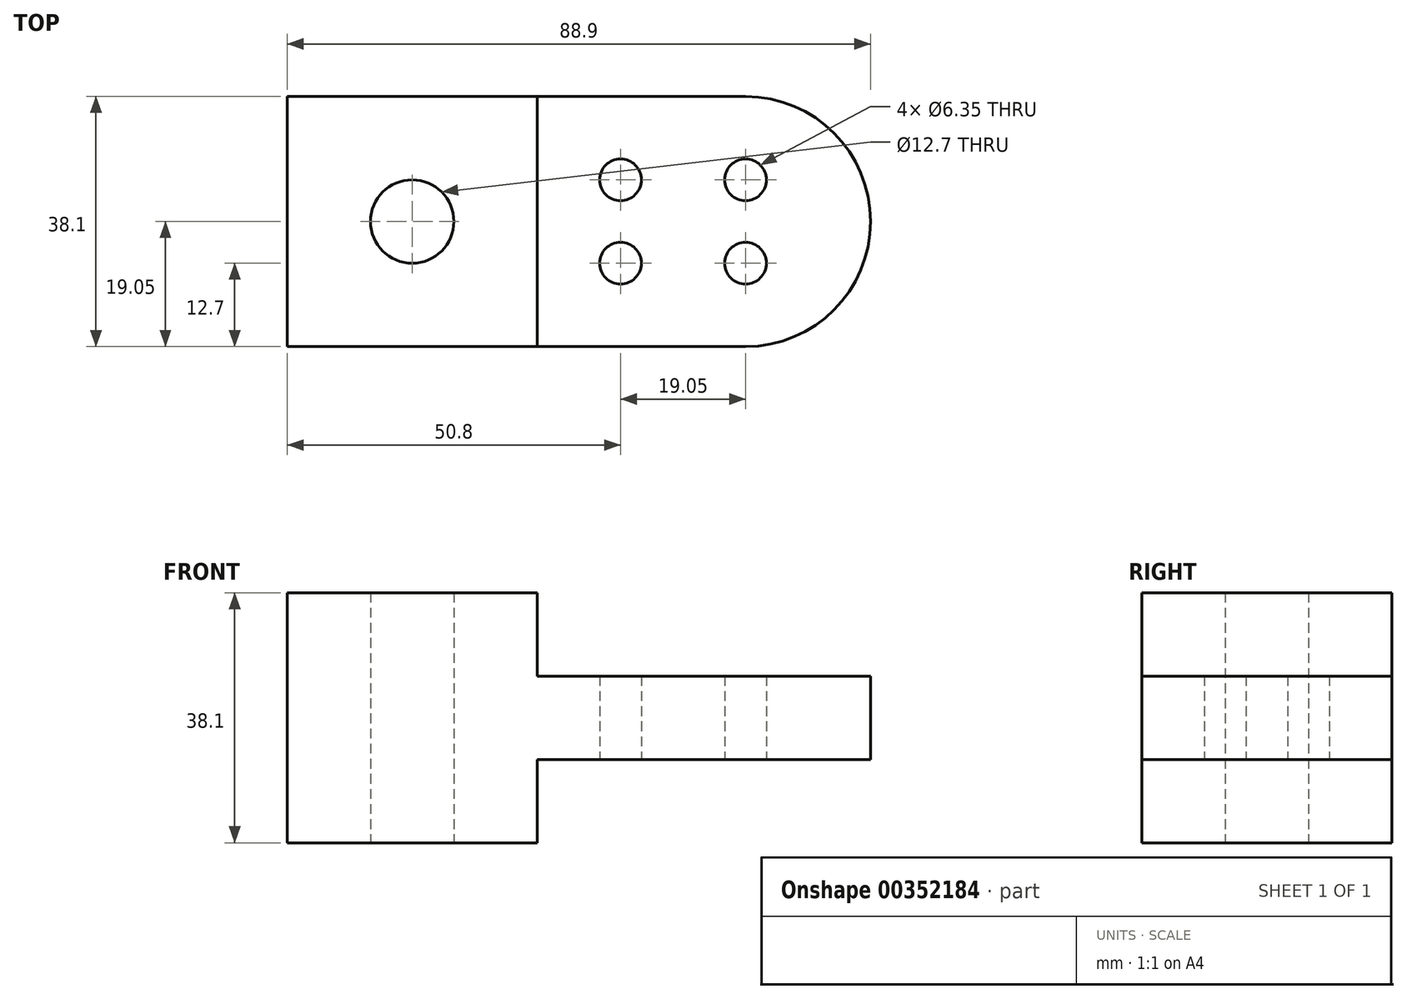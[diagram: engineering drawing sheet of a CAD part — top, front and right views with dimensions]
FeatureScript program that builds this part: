
annotation { "Feature Type Name" : "Feature", "Feature Type Description" : "" }
export const myFeature = defineFeature(function(context is Context, id is Id, definition is map)
    precondition{}
    {
        {
            var Q0;
            Q0=qCreatedBy(makeId("Top.planeOp"),FACE);
            var sketch = newSketch(context, id + "F0", { "sketchPlane" : qUnion([Q0])});
            skLineSegment(sketch, "E0.bottom", {"start": v(-38.1, 19.05) * mm, "end": v(0, 19.05) * mm});
            skLineSegment(sketch, "E0.top", {"start": v(-38.1, -19.05) * mm, "end": v(0, -19.05) * mm});
            skLineSegment(sketch, "E0.left", {"start": v(-38.1, 19.05) * mm, "end": v(-38.1, -19.05) * mm});
            skLineSegment(sketch, "E0.right", {"start": v(0, 19.05) * mm, "end": v(0, -19.05) * mm});
            skLineSegment(sketch, "E1", {"start": v(0, 19.05) * mm, "end": v(31.75, 19.05) * mm});
            skLineSegment(sketch, "E2", {"start": v(0, -19.05) * mm, "end": v(31.75, -19.05) * mm});
            skArc(sketch, "E3", {"start": v(31.75, 19.05) * mm, "mid": v(50.8, 0) * mm, "end": v(31.75, -19.05) * mm});
            skCircle(sketch, "E4", {"center": v(-19.05, 0) * mm, "radius": 6.35 * mm});
            skCircle(sketch, "E5", {"center": v(12.7, 6.35) * mm, "radius": 3.18 * mm});
            skCircle(sketch, "E6", {"center": v(31.75, 6.35) * mm, "radius": 3.18 * mm});
            skCircle(sketch, "E7", {"center": v(12.7, -6.35) * mm, "radius": 3.18 * mm});
            skCircle(sketch, "E8", {"center": v(31.75, -6.35) * mm, "radius": 3.18 * mm});
            skSolve(sketch);
        }
        {
            var Q0;
            Q0=makeQuery(id+"F0.imprint","IMPRINT",FACE,{"disambiguationData":[TD([[makeQuery(id+"F0.imprint","IMPRINT",EDGE,{"derivedFrom":sQuery(id+"F0.wireOp",EDGE,"E0.bottom")}),-1.0]])]});
            extrude(context, id + "F1", {"entities" : qUnion([Q0]), "endBound" : BoundingType.SYMMETRIC, "depth" : 38.1 * mm});
        }
        {
            var Q0;
            Q0 = qSketchRegion(id + "F0", true);
            extrude(context, id + "F2", {"entities" : qUnion([Q0]), "operationType" : NewBodyOperationType.ADD, "endBound" : BoundingType.SYMMETRIC, "depth" : 12.7 * mm});
        }
    });
